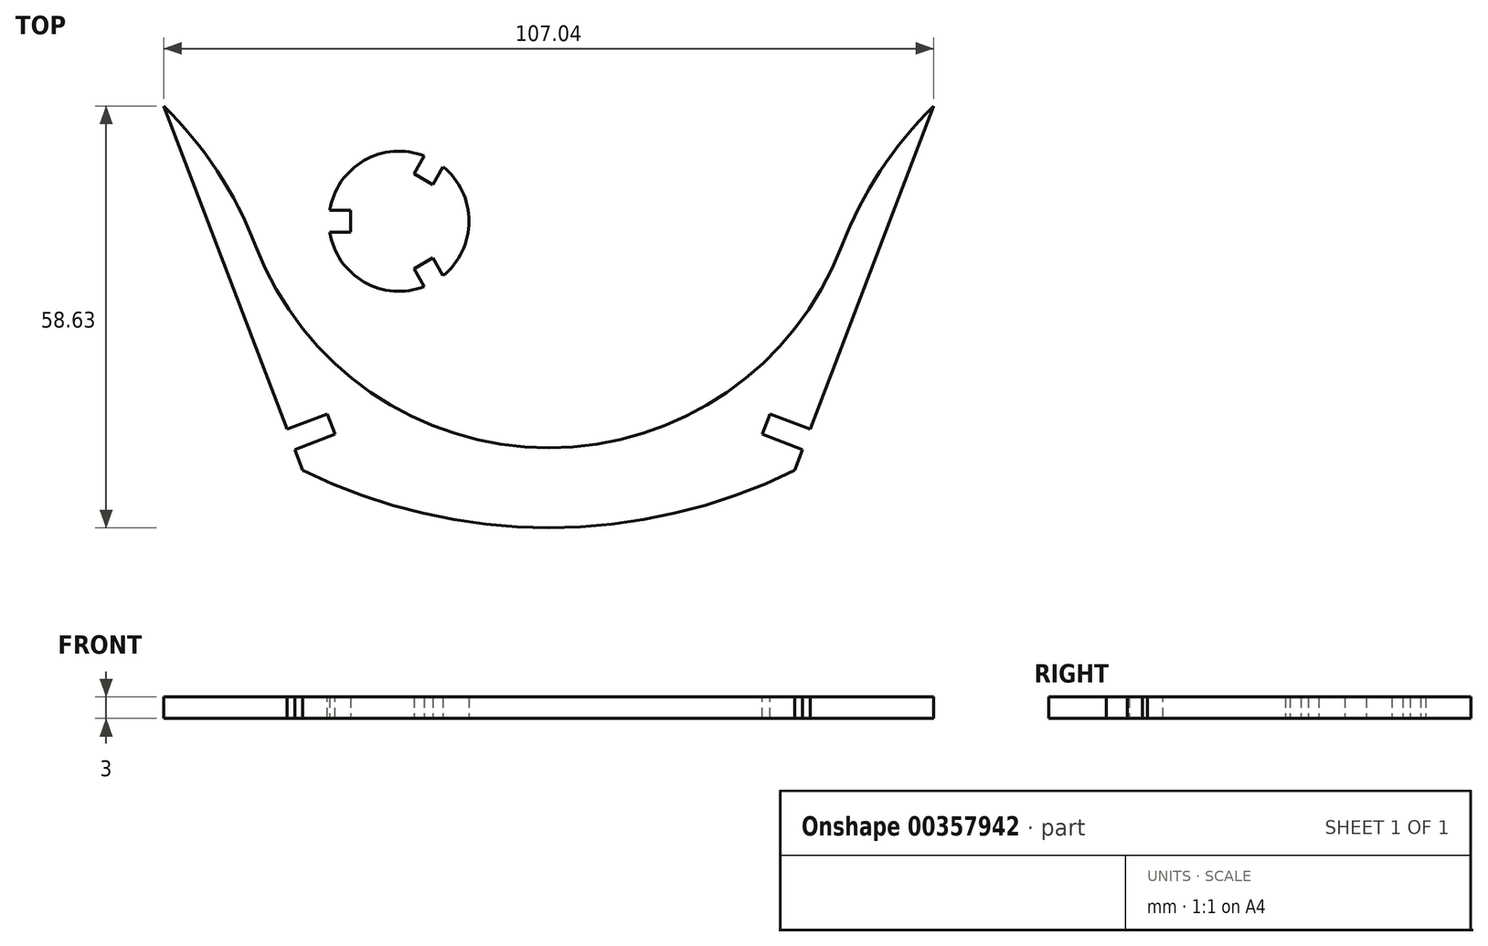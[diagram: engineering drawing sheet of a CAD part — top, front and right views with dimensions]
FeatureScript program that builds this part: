
annotation { "Feature Type Name" : "Feature", "Feature Type Description" : "" }
export const myFeature = defineFeature(function(context is Context, id is Id, definition is map)
    precondition{}
    {
        {
            var Q0;
            Q0=qCreatedBy(makeId("Top.planeOp"),FACE);
            var sketch = newSketch(context, id + "F0", { "sketchPlane" : qUnion([Q0])});
            skLineSegment(sketch, "E0", {"start": v(-53.52, 70.13) * mm, "end": v(0, -70) * mm, "construction": true});
            skLineSegment(sketch, "E1", {"start": v(0, -70) * mm, "end": v(0, 80) * mm, "construction": true});
            skArc(sketch, "E2", {"start": v(0, 80) * mm, "mid": v(-27.21, 77.51) * mm, "end": v(-53.52, 70.13) * mm, "construction": true});
            skArc(sketch, "E3", {"start": v(-40.74, 50.68) * mm, "mid": v(-46.08, 61.1) * mm, "end": v(-53.52, 70.13) * mm});
            skArc(sketch, "E4", {"start": v(-40.74, 50.68) * mm, "mid": v(-24.73, 30.32) * mm, "end": v(0, 22.63) * mm});
            skLineSegment(sketch, "E5", {"start": v(0, 22.63) * mm, "end": v(0, 22.63) * mm});
            skLineSegment(sketch, "E6", {"start": v(-4.3, 22.63) * mm, "end": v(7.92, 22.63) * mm, "construction": true});
            skLineSegment(sketch, "E7", {"start": v(-48.82, 71.83) * mm, "end": v(-29.15, 20.32) * mm, "construction": true});
            skArc(sketch, "E8", {"start": v(-34.18, 19.48) * mm, "mid": v(-17.55, 13.52) * mm, "end": v(0, 11.5) * mm});
            skLineSegment(sketch, "E9", {"start": v(-53.52, 70.13) * mm, "end": v(-34.18, 19.48) * mm});
            skLineSegment(sketch, "E10", {"start": v(0, 22.63) * mm, "end": v(0, 11.5) * mm});
            skLineSegment(sketch, "E11", {"start": v(-11, 11.5) * mm, "end": v(62.93, 11.5) * mm, "construction": true});
            skSolve(sketch);
        }
        {
            var Q0;
            Q0=makeQuery(id+"F0.imprint","IMPRINT",FACE,{"disambiguationData":[TD([[makeQuery(id+"F0.imprint","IMPRINT",EDGE,{"derivedFrom":sQuery(id+"F0.wireOp",EDGE,"E3")}),1.0]])]});
            extrude(context, id + "F1", {"entities" : qUnion([Q0]), "depth" : 3 * mm});
        }
        {
            var Q0;
            {var subQ0=makeQuery(id+"F1.opExtrude","CAP_FACE",FACE,{"disambiguationData":[OSD([sQuery(id+"F0.wireOp",EDGE,"E3"),sQuery(id+"F0.wireOp",EDGE,"E4"),sQuery(id+"F0.wireOp",EDGE,"E8"),sQuery(id+"F0.wireOp",EDGE,"E9"),sQuery(id+"F0.wireOp",EDGE,"E10")])],"isStart":false});Q0=makeQuery(id+"F4.boolean.opBoolean","MERGE",FACE,{"derivedFrom":[subQ0,makeQuery(id+"F4.opPattern","COPY",FACE,{"derivedFrom":subQ0,"instanceName":"1"})]});}
            var sketch = newSketch(context, id + "F2", { "sketchPlane" : qUnion([Q0])});
            skLineSegment(sketch, "E12.bottom", {"start": v(-29.68, 24.52) * mm, "end": v(-35.29, 22.38) * mm});
            skLineSegment(sketch, "E12.top", {"start": v(-30.75, 27.32) * mm, "end": v(-36.36, 25.18) * mm});
            skLineSegment(sketch, "E12.left", {"start": v(-29.68, 24.52) * mm, "end": v(-30.75, 27.32) * mm});
            skLineSegment(sketch, "E12.right", {"start": v(-35.29, 22.38) * mm, "end": v(-36.36, 25.18) * mm});
            skPoint(sketch, "E12.middle", {"position": v(-33.02, 24.85) * mm});
            skSolve(sketch);
        }
        {
            var Q0;
            Q0=makeQuery(id+"F2.imprint","IMPRINT",FACE,{"disambiguationData":[TD([[makeQuery(id+"F2.imprint","IMPRINT",EDGE,{"derivedFrom":sQuery(id+"F2.wireOp",EDGE,"E12.bottom")}),-1.0]])]});
            extrude(context, id + "F3", {"entities" : qUnion([Q0]), "operationType" : NewBodyOperationType.REMOVE, "oppositeDirection" : true, "depth" : 25 * mm});
        }
        {
            var Q0;
            Q0=makeQuery(id+"F1.opExtrude","SWEPT_BODY",BODY,{"disambiguationData":[OSD([sQuery(id+"F0.wireOp",EDGE,"E3"),sQuery(id+"F0.wireOp",EDGE,"E4"),sQuery(id+"F0.wireOp",EDGE,"E5"),sQuery(id+"F0.wireOp",EDGE,"E8"),sQuery(id+"F0.wireOp",EDGE,"E9"),sQuery(id+"F0.wireOp",EDGE,"E10")])]});
            var Q1;
            Q1=makeQuery(id+"F1.opExtrude","SWEPT_FACE",FACE,{"disambiguationData":[OSD([sQuery(id+"F0.wireOp",EDGE,"E10")])]});
            mirror(context, id + "F4", {"operationType" : NewBodyOperationType.ADD, "entities" : qUnion([Q0]), "mirrorPlane" : qUnion([Q1])});
        }
        {
            var Q0;
            Q0=qCreatedBy(makeId("Top.planeOp"),FACE);
            var sketch = newSketch(context, id + "F5", { "sketchPlane" : qUnion([Q0])});
            skCircle(sketch, "E13", {"center": v(-20.8, 54.1) * mm, "radius": 9.74 * mm});
            skLineSegment(sketch, "E14.bottom", {"start": v(-27.54, 52.6) * mm, "end": v(-33.54, 52.6) * mm});
            skLineSegment(sketch, "E14.top", {"start": v(-27.54, 55.6) * mm, "end": v(-33.54, 55.6) * mm});
            skLineSegment(sketch, "E14.left", {"start": v(-27.54, 52.6) * mm, "end": v(-27.54, 55.6) * mm});
            skLineSegment(sketch, "E14.right", {"start": v(-33.54, 52.6) * mm, "end": v(-33.54, 55.6) * mm});
            skPoint(sketch, "E14.middle", {"position": v(-30.54, 54.1) * mm});
            skLineSegment(sketch, "E15", {"start": v(-30.54, 58.14) * mm, "end": v(-30.54, 48.76) * mm});
            skCircle(sketch, "E16", {"center": v(-20.8, 54.1) * mm, "radius": 6.74 * mm, "construction": true});
            skCircle(sketch, "E17", {"center": v(-20.8, 54.1) * mm, "radius": 1.48 * mm, "construction": true});
            skLineSegment(sketch, "E18", {"start": v(-21.54, 55.38) * mm, "end": v(-21.54, 52.82) * mm, "construction": true});
            skLineSegment(sketch, "E19", {"start": v(-21.54, 52.82) * mm, "end": v(-19.33, 54.1) * mm, "construction": true});
            skLineSegment(sketch, "E20", {"start": v(-19.33, 54.1) * mm, "end": v(-21.54, 55.38) * mm, "construction": true});
            skLineSegment(sketch, "E21.1.0", {"start": v(-18.73, 47.52) * mm, "end": v(-15.73, 42.32) * mm});
            skLineSegment(sketch, "E21.1.1", {"start": v(-16.14, 49.02) * mm, "end": v(-18.73, 47.52) * mm});
            skLineSegment(sketch, "E21.1.2", {"start": v(-13.14, 43.82) * mm, "end": v(-15.73, 42.32) * mm});
            skLineSegment(sketch, "E21.1.3", {"start": v(-16.14, 49.02) * mm, "end": v(-13.14, 43.82) * mm});
            skLineSegment(sketch, "E21.2.0", {"start": v(-16.14, 59.19) * mm, "end": v(-13.14, 64.38) * mm});
            skLineSegment(sketch, "E21.2.1", {"start": v(-18.73, 60.69) * mm, "end": v(-16.14, 59.19) * mm});
            skLineSegment(sketch, "E21.2.2", {"start": v(-15.73, 65.88) * mm, "end": v(-13.14, 64.38) * mm});
            skLineSegment(sketch, "E21.2.3", {"start": v(-18.73, 60.69) * mm, "end": v(-15.73, 65.88) * mm});
            skSolve(sketch);
        }
        {
            var Q0;
            {var subQ1=sQuery(id+"F5.wireOp",EDGE,"E14.left");Q0=makeQuery(id+"F5.imprint","IMPRINT",FACE,{"disambiguationData":[TD([[makeQuery(id+"F5.imprint","IMPRINT",EDGE,{"derivedFrom":subQ1}),-1.0]])]});}
            extrude(context, id + "F6", {"entities" : qUnion([Q0]), "depth" : 3 * mm});
        }
    });
